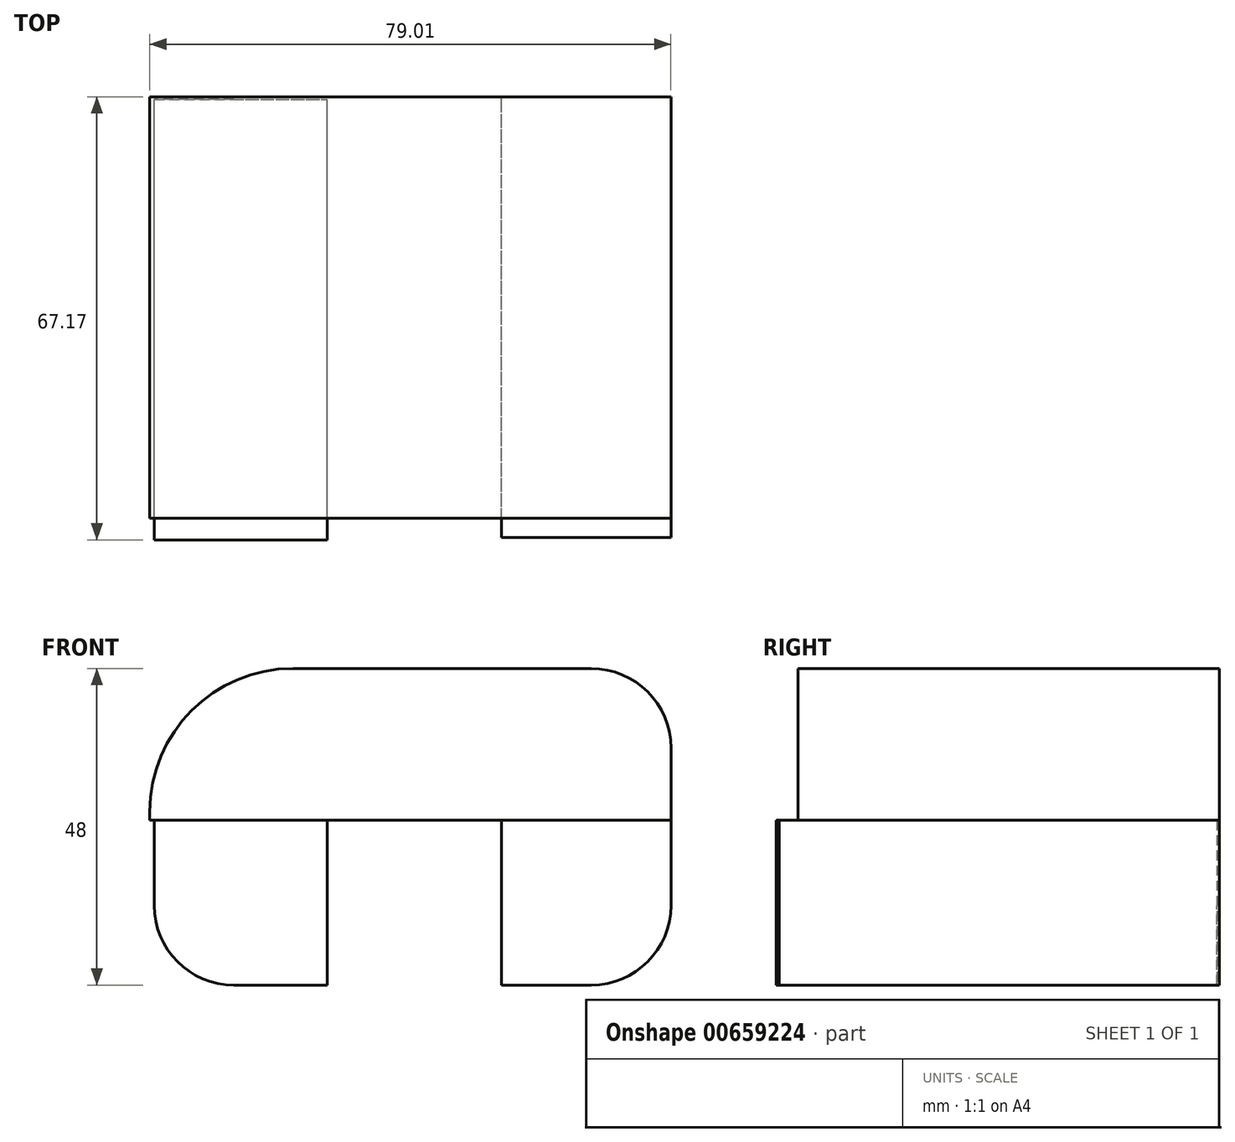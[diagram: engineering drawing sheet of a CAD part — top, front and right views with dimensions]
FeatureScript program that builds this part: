
annotation { "Feature Type Name" : "Feature", "Feature Type Description" : "" }
export const myFeature = defineFeature(function(context is Context, id is Id, definition is map)
    precondition{}
    {
        {
            var Q0;
            Q0=qCreatedBy(makeId("Top.planeOp"),FACE);
            var sketch = newSketch(context, id + "F0", { "sketchPlane" : qUnion([Q0])});
            skLineSegment(sketch, "E0.bottom", {"start": v(-52.67, -41.73) * mm, "end": v(-26.45, -41.73) * mm});
            skLineSegment(sketch, "E0.top", {"start": v(-52.67, 25.03) * mm, "end": v(-26.45, 25.03) * mm});
            skLineSegment(sketch, "E0.left", {"start": v(-52.67, -41.73) * mm, "end": v(-52.67, 25.03) * mm});
            skLineSegment(sketch, "E0.right", {"start": v(-26.45, -41.73) * mm, "end": v(-26.45, 25.03) * mm});
            skLineSegment(sketch, "E1.bottom", {"start": v(-0.03, -41.34) * mm, "end": v(25.66, -41.34) * mm});
            skLineSegment(sketch, "E1.top", {"start": v(-0.03, 25.44) * mm, "end": v(25.66, 25.44) * mm});
            skLineSegment(sketch, "E1.left", {"start": v(-0.03, -41.34) * mm, "end": v(-0.03, 25.44) * mm});
            skLineSegment(sketch, "E1.right", {"start": v(25.66, -41.34) * mm, "end": v(25.66, 25.44) * mm});
            skSolve(sketch);
        }
        {
            var Q0;
            Q0 = qSketchRegion(id + "F0", true);
            extrude(context, id + "F1", {"entities" : qUnion([Q0]), "depth" : 25 * mm, "offsetDistance" : 25 * mm});
        }
        {
            var Q0;
            Q0=makeQuery(id+"F1.opExtrude","CAP_FACE",FACE,{"disambiguationData":[OSD([sQuery(id+"F0.wireOp",EDGE,"E1.bottom"),sQuery(id+"F0.wireOp",EDGE,"E1.top"),sQuery(id+"F0.wireOp",EDGE,"E1.left"),sQuery(id+"F0.wireOp",EDGE,"E1.right")])],"isStart":false});
            var sketch = newSketch(context, id + "F2", { "sketchPlane" : qUnion([Q0])});
            skLineSegment(sketch, "E2.bottom", {"start": v(-53.35, -38.46) * mm, "end": v(25.66, -38.46) * mm});
            skLineSegment(sketch, "E2.top", {"start": v(-53.35, 25.44) * mm, "end": v(25.66, 25.44) * mm});
            skLineSegment(sketch, "E2.left", {"start": v(-53.35, -38.46) * mm, "end": v(-53.35, 25.44) * mm});
            skLineSegment(sketch, "E2.right", {"start": v(25.66, -38.46) * mm, "end": v(25.66, 25.44) * mm});
            skSolve(sketch);
        }
        {
            var Q0;
            Q0 = qSketchRegion(id + "F2", true);
            extrude(context, id + "F3", {"entities" : qUnion([Q0]), "depth" : 23 * mm, "offsetDistance" : 25 * mm});
        }
        {
            var Q0;
            Q0=makeQuery(id+"F3.opExtrude","CAP_EDGE",EDGE,{"disambiguationData":[OSD([sQuery(id+"F2.wireOp",EDGE,"E2.left")])],"isStart":false});
            fillet(context, id + "F4", {"entities" : qUnion([Q0]), "radius" : 21.73 * mm, "tangentPropagation" : true, "allowEdgeOverflow" : false});
        }
        {
            var Q0;
            Q0=makeQuery(id+"F3.opExtrude","CAP_EDGE",EDGE,{"disambiguationData":[OSD([sQuery(id+"F2.wireOp",EDGE,"E2.right")])],"isStart":false});
            var Q1;
            Q1=makeQuery(id+"F1.opExtrude","CAP_EDGE",EDGE,{"disambiguationData":[OSD([sQuery(id+"F0.wireOp",EDGE,"E0.left")])],"isStart":true});
            var Q2;
            Q2=makeQuery(id+"F1.opExtrude","CAP_EDGE",EDGE,{"disambiguationData":[OSD([sQuery(id+"F0.wireOp",EDGE,"E1.right")])],"isStart":true});
            fillet(context, id + "F5", {"entities" : qUnion([Q0, Q1, Q2]), "radius" : 12.07 * mm, "tangentPropagation" : true, "allowEdgeOverflow" : false});
        }
    });
